# Revit family: Shower-Wall_Supply_Elbow-KOHLER-EXHALE-K-98354T_1
name_source: partatom
category: Plumbing Fixtures
revit_build: Autodesk Revit 2017 (Build: 20160225_1515(x64)
units: mm (PartAtom-declared; Revit-internal decimal feet)

## family parameters
Cut with Voids When Loaded = No
Host = Face
OmniClass Number = 23.31.25.00
OmniClass Title = Toilet and Bath Specialties
Part Type = Normal
Room Calculation Point = No
Round Connector Dimension = Use Diameter
Shared = No

## types (3) — shared parameters
ADA Compliant = No
Assembly Code = C1030200
CW Connection = No
Cold Water Inlet = Cold Water Inlet
Date Modified = 07/03/2020
Default Elevation = 42"
Description = Free rain shower bracket (direct water inlet)
Drain Included = No
Flow Rate = 0 GPM
HW Connection = Yes
Height = 2"
Hot Water Inlet = Tempered Water Inlet
Length = 2 3/4"
Manufacturer = KOHLER Co.
Master Format 2014 = 22 42 23
Master Format 2014 Name = Residential Showers
Material = Premium Metal Construction
Pressure = 0.00 psi
Product Documentation Link = http://files.kohler.com.cn
Product Name = EXHALE
Product Page URL = http://www.kohler.com.cn
URL = http://www.kohler.com.cn
Vent Connection = No
Waste Connection = No
Waste Water Connection = Waste Water Connection
WaterSense Certified = No
Width = 2"

## per-type parameters (varying)
| type | Finish | Model | Type |
| CP-Polished Chrome | Kohler-Metal-CP-Polished_Chrome | K-98354T-CP | 1 |
| TT-Titanium Silver | Kohler-Metal-TT-Titanium_Silver | K-98354T-TT | 3 |
| AF-Flange Gold | Kohler-Metal-AF-Flange_Gold | K-98354T-AF | 2 |

## geometry (parser evidence)
native form markers: Sweep x6
no freeform markers — native parametric forms only
